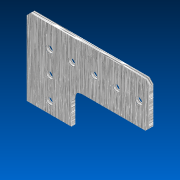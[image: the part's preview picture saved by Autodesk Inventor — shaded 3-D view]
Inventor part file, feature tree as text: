
AUTODESK INVENTOR PART (.ipt)
format: ipt  version: 2022.2 (Build 262287000, 287)  size: 148,992 bytes
history: native  units: in
note: dims shown in document units (in); Inventor stores cm internally (conversion verified against a paired STEP export)
features: extrude x1, sketch x1, other x1
ambient origin geometry x8: Origin, YZ Plane, XZ Plane, XY Plane, X Axis, Y Axis, Z Axis, Center Point
bodies: Solid1 (feature_tree)
feature tree (3):
  extrude  "Extrusion1"  TaperAngle=0.0deg  [1 undecoded]
  sketch  "Sketch1"  dims[d0=1.25in d1=0.0in d2=0.0in]
  other  "Break-Corner1"
note: 1 required parameter value undecoded (feature->parameter linkage not recoverable at this tier; creation-order binding heuristic only, values carry confidence <= 0.55)
